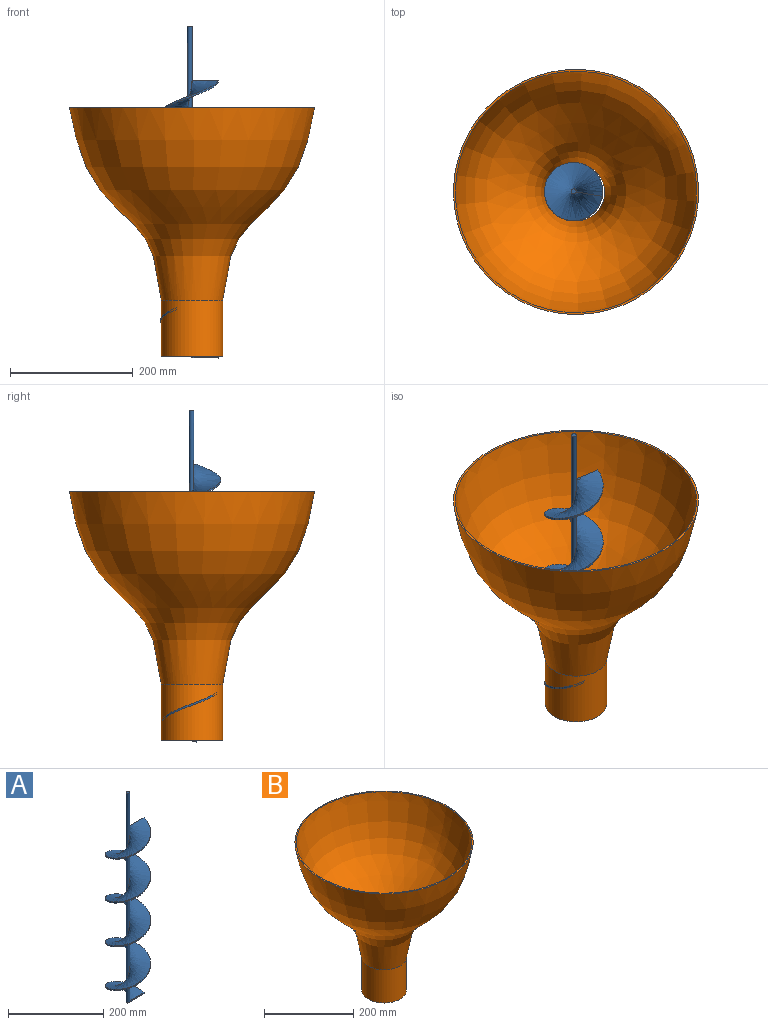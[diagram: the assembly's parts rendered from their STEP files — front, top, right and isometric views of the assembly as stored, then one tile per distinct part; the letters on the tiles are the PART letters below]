
ASSEMBLY  parts=2 mates=1
PART A: 13 faces, bbox 95x95x541.8 mm
  f0: cylinder r=4mm len=201.3mm, axis (0,0,-1), area 3645.4mm2, adj f1,f6,f8,f12
  f1: cylinder r=4mm len=222mm, axis (0,0,-1), area 2752mm2, adj f0,f2,f8,f10
  f2: cylinder r=4mm len=222mm, axis (0,0,-1), area 2752mm2, adj f1,f3,f8,f10
  f3: cylinder r=4mm len=222mm, axis (0,0,-1), area 2752mm2, adj f2,f4,f8,f10
  f4: cylinder r=4mm len=109.5mm, axis (0,0,-1), area 1339.3mm2, adj f3,f5,f10
  f5: plane 8x8mm, normal (0,0,-1), area 50.3mm2, adj f4,f9
  f6: plane 43.5x3mm, normal (0,1,0), area 130.5mm2, adj f0,f8,f10,f11
  f7: plane 43.5x3mm, normal (0,-1,0), area 130.5mm2, adj f8,f9,f10,f11
  f8: bspline ~450x95mm, area 35344.4mm2, adj f0,f1,f2,f3,f6,f7,f11
  f9: cylinder r=4mm len=3mm, axis (0,0,-1), area 1mm2, adj f5,f7,f10
  f10: bspline ~450x95mm, area 35356.4mm2, adj f1,f2,f3,f4,f6,f7,f9,f11
  f11: cylinder r=47.5mm len=453mm, axis (0,0,-1), area 3581.4mm2, adj f6,f7,f8,f10
  f12: plane 8x8mm, normal (0,0,1), area 50.3mm2, adj f0
PART B: 6 faces, bbox 400x400x405.6 mm
  f0: plane 100x100mm, normal (0,0,-1), area 914.2mm2, adj f1,f4
  f1: cylinder r=50mm len=100mm, axis (0,0,1), area 28610.5mm2, adj f0,f2
  f2: revolved ~400x400mm, area 281734.6mm2, adj f1,f3
  f3: plane 400x400mm, normal (0,0,1), area 3777.8mm2, adj f2,f5
  f4: cylinder r=47mm len=94mm, axis (0,0,1), area 26940.4mm2, adj f0,f5
  f5: revolved ~393.94x393.94mm, area 274160.9mm2, adj f3,f4
PLACE A rot(axis=(0,0,-1),10deg) t=(-324.42,-103.7,111.62)mm
PLACE B rot(axis=(0,0,1),30.8deg) t=(-320.45,-104.35,202.69)mm
MATE revolute A.f5 <-> B.f1  axis (0,0,1) through (-320.48,-104.39,111.62)mm
